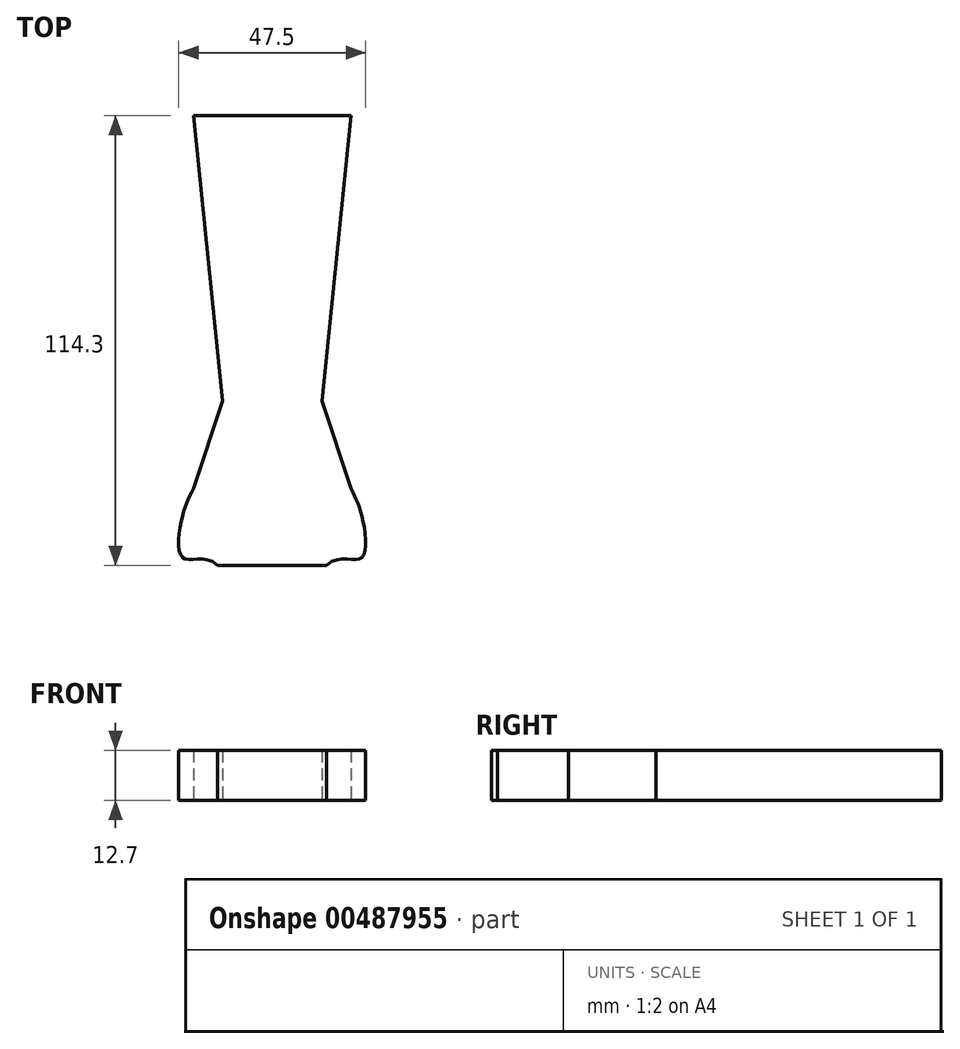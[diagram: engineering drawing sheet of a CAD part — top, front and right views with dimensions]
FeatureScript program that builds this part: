
annotation { "Feature Type Name" : "Feature", "Feature Type Description" : "" }
export const myFeature = defineFeature(function(context is Context, id is Id, definition is map)
    precondition{}
    {
        {
            var Q0;
            Q0=qCreatedBy(makeId("Top.planeOp"),FACE);
            var sketch = newSketch(context, id + "F0", { "sketchPlane" : qUnion([Q0])});
            skLineSegment(sketch, "E0", {"start": v(-20, 52.04) * mm, "end": v(0, 52.04) * mm});
            skLineSegment(sketch, "E1.MirrorCS", {"start": v(20, 52.04) * mm, "end": v(0, 52.04) * mm});
            skLineSegment(sketch, "E2", {"start": v(-20, 52.04) * mm, "end": v(-12.63, -20.45) * mm});
            skLineSegment(sketch, "E3", {"start": v(-12.63, -20.45) * mm, "end": v(-20, -42.71) * mm});
            skFitSpline(sketch, "E4", {"points": [v(-20, -42.71) * mm, v(-22.86, -49.93) * mm, v(-22.56, -60.46) * mm, v(-13.84, -62.26) * mm], "startDerivative": vector(-11.5, -23.63) * mm, "endDerivative": vector(28.11, -27.7) * mm});
            skLineSegment(sketch, "E5", {"start": v(-13.84, -62.26) * mm, "end": v(0, -62.26) * mm});
            skLineSegment(sketch, "E6.MirrorCS", {"start": v(20, 52.04) * mm, "end": v(12.63, -20.45) * mm});
            skLineSegment(sketch, "E7.MirrorCS", {"start": v(12.63, -20.45) * mm, "end": v(20, -42.71) * mm});
            skFitSpline(sketch, "E8.MirrorCS", {"points": [v(20, -42.71) * mm, v(22.86, -49.93) * mm, v(22.56, -60.46) * mm, v(13.84, -62.26) * mm], "startDerivative": vector(11.5, -23.63) * mm, "endDerivative": vector(-28.11, -27.7) * mm});
            skLineSegment(sketch, "E9.MirrorCS", {"start": v(13.84, -62.26) * mm, "end": v(0, -62.26) * mm});
            skSolve(sketch);
        }
        {
            var Q0;
            Q0=makeQuery(id+"F0.imprint","IMPRINT",FACE,{"disambiguationData":[TD([[makeQuery(id+"F0.imprint","IMPRINT",EDGE,{"derivedFrom":sQuery(id+"F0.wireOp",EDGE,"E0")}),-1.0]])]});
            extrude(context, id + "F1", {"entities" : qUnion([Q0]), "depth" : 12.7 * mm});
        }
    });
